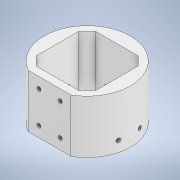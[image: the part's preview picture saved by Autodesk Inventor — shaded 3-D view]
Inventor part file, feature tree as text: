
AUTODESK INVENTOR PART (.ipt)
format: ipt  version: 2021 (Build 250183000, 183)  size: 154,624 bytes
history: native  units: mm
features: extrude x5, sketch x5, other x1
ambient origin geometry x8: Origin, YZ Plane, XZ Plane, XY Plane, X Axis, Y Axis, Z Axis, Center Point
bodies: Body1 (feature_tree)
feature tree (11):
  other  "Sólido1"
  extrude  "Extrusión1"  Depth=40.0mm TaperAngle=0.0deg
  extrude  "Extrusión10"  Depth=3.0mm
  extrude  "Extrusión11"  Depth=3.0mm
  extrude  "Extrusión12"  Depth=200.0mm TaperAngle=0.0deg
  extrude  "Extrusión13"  Depth=3.0mm
  sketch  "Boceto1"  dims[d10=40.0mm d11=0.0mm d75=40.0mm d76=0.0mm]
  sketch  "Boceto14"  dims[d80=3.0mm d81=3.0mm]
  sketch  "Boceto15"  dims[d82=200.0mm d83=0.0mm d88=3.0mm]
  sketch  "Boceto16"  dims[d89=3.0mm d90=200.0mm d91=0.0mm]
  sketch  "Boceto17"  dims[d95=3.0mm d96=3.0mm d97=200.0mm d98=0.0mm d67=0.5mm d68=0.872665mm d69=0.5mm d70=0.872665mm]
